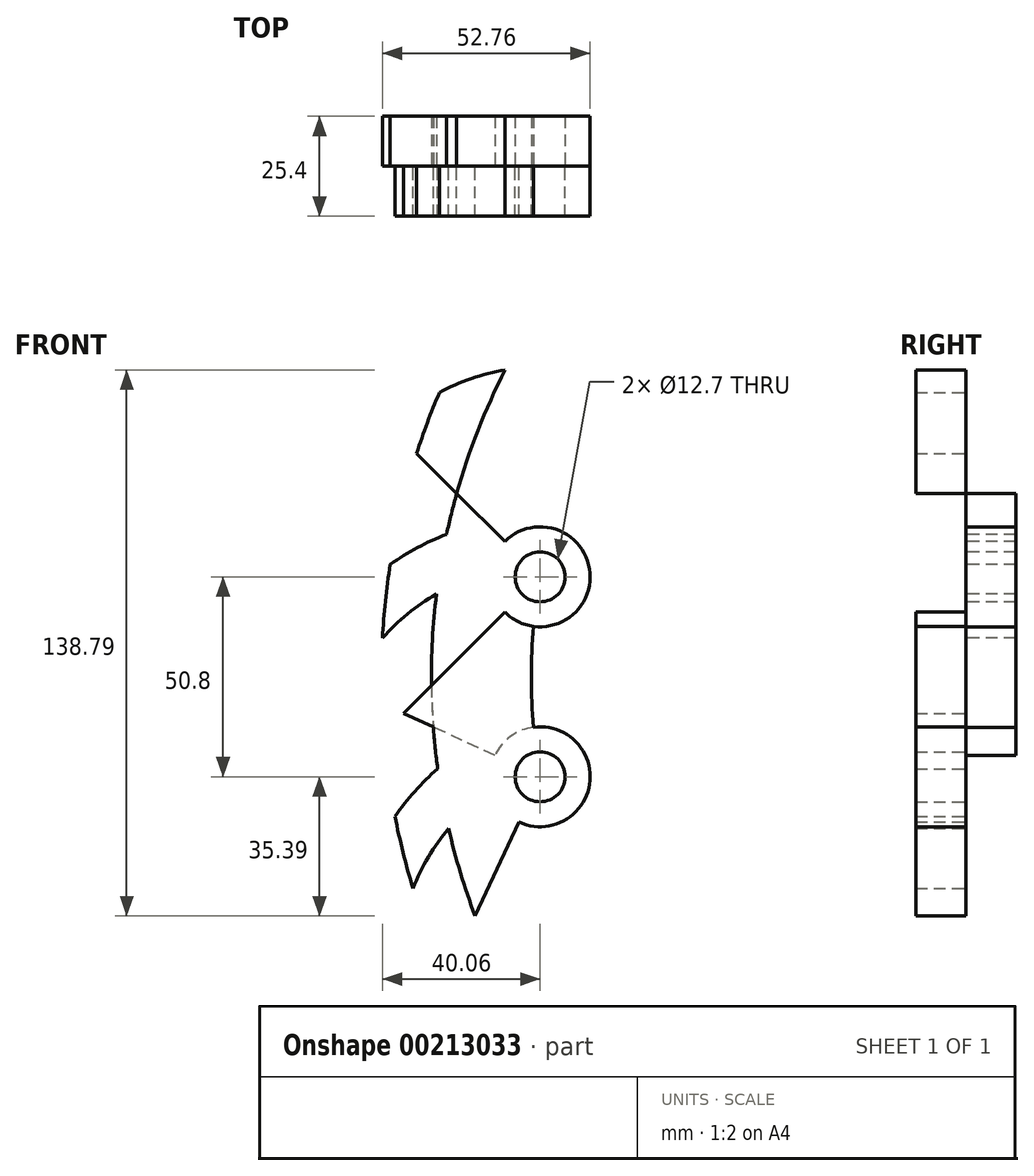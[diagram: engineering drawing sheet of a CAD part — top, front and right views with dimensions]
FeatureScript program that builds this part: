
annotation { "Feature Type Name" : "Feature", "Feature Type Description" : "" }
export const myFeature = defineFeature(function(context is Context, id is Id, definition is map)
    precondition{}
    {
        {
            var Q0;
            Q0=qCreatedBy(makeId("Front.planeOp"),FACE);
            var sketch = newSketch(context, id + "F0", { "sketchPlane" : qUnion([Q0])});
            skCircle(sketch, "E0", {"center": v(0, 0) * mm, "radius": 12.7 * mm});
            skCircle(sketch, "E1", {"center": v(0, 50.8) * mm, "radius": 12.7 * mm});
            skArc(sketch, "E2", {"start": v(0, 50.8) * mm, "mid": v(0, 0) * mm, "end": v(17.37, -47.74) * mm});
            skLineSegment(sketch, "E3", {"start": v(0, 50.8) * mm, "end": v(144.05, 25.4) * mm, "construction": true});
            skLineSegment(sketch, "E4", {"start": v(144.05, 25.4) * mm, "end": v(0, 0) * mm, "construction": true});
            skLineSegment(sketch, "E5", {"start": v(144.05, 25.4) * mm, "end": v(-15.62, -66.79) * mm, "construction": true});
            skArc(sketch, "E6", {"start": v(-4.62, -60.44) * mm, "mid": v(-11.07, -48.15) * mm, "end": v(-16.5, -35.39) * mm, "construction": true});
            skArc(sketch, "E7", {"start": v(-15.62, -66.79) * mm, "mid": v(-19.88, -58.97) * mm, "end": v(-23.76, -50.96) * mm, "construction": true});
            skLineSegment(sketch, "E8", {"start": v(0, 0) * mm, "end": v(0, 50.8) * mm, "construction": true});
            skLineSegment(sketch, "E9", {"start": v(0, 50.8) * mm, "end": v(-58.55, 109.35) * mm});
            skLineSegment(sketch, "E10", {"start": v(0, 50.8) * mm, "end": v(-62.14, -11.34) * mm});
            skLineSegment(sketch, "E11", {"start": v(0, 0) * mm, "end": v(-80.33, 37.46) * mm});
            skLineSegment(sketch, "E12", {"start": v(0, 0) * mm, "end": v(-37.7, -80.86) * mm});
            skArc(sketch, "E13", {"start": v(-21.18, 71.98) * mm, "mid": v(-15.8, 88) * mm, "end": v(-8.88, 103.4) * mm});
            skArc(sketch, "E14", {"start": v(-16.5, -35.39) * mm, "mid": v(-27.46, 17.92) * mm, "end": v(-21.18, 71.98) * mm});
            skArc(sketch, "E15", {"start": v(-31.37, 82.17) * mm, "mid": v(-25.13, 98.68) * mm, "end": v(-17.35, 114.52) * mm});
            skArc(sketch, "E16", {"start": v(-23.76, -50.96) * mm, "mid": v(-40.02, 14.89) * mm, "end": v(-31.37, 82.17) * mm});
            skArc(sketch, "E17", {"start": v(-32.32, -28.34) * mm, "mid": v(-28.41, -20.37) * mm, "end": v(-23.24, -13.16) * mm});
            skArc(sketch, "E18", {"start": v(-36.88, -10.08) * mm, "mid": v(-31.83, -3.68) * mm, "end": v(-26.03, 2.04) * mm});
            skArc(sketch, "E19.1.0", {"start": v(-40.06, 35.22) * mm, "mid": v(-33.66, 41.37) * mm, "end": v(-26.33, 46.39) * mm});
            skArc(sketch, "E19.1.1", {"start": v(-38.1, 53.94) * mm, "mid": v(-31.17, 58.22) * mm, "end": v(-23.76, 61.62) * mm});
            skArc(sketch, "E19.2.0", {"start": v(-25.6, 97.6) * mm, "mid": v(-17.48, 101.2) * mm, "end": v(-8.88, 103.4) * mm});
            skArc(sketch, "E19.2.1", {"start": v(-17.35, 114.52) * mm, "mid": v(-9.37, 116.17) * mm, "end": v(-1.25, 116.83) * mm});
            skLineSegment(sketch, "E19.anchor1", {"start": v(144.05, 25.4) * mm, "end": v(-32.32, -28.34) * mm, "construction": true});
            skLineSegment(sketch, "E19.anchor2", {"start": v(144.05, 25.4) * mm, "end": v(-25.6, 97.6) * mm, "construction": true});
            skArc(sketch, "E20", {"start": v(-8.88, 103.4) * mm, "mid": v(-5.22, 110.2) * mm, "end": v(-1.25, 116.83) * mm});
            skArc(sketch, "E21", {"start": v(-17.35, 114.52) * mm, "mid": v(-9.23, 127.87) * mm, "end": v(0, 140.48) * mm, "construction": true});
            skArc(sketch, "E22", {"start": v(-1.25, 116.83) * mm, "mid": v(8.95, 131.32) * mm, "end": v(20.6, 144.69) * mm, "construction": true});
            skCircle(sketch, "E23", {"center": v(0, 0) * mm, "radius": 6.35 * mm});
            skCircle(sketch, "E24", {"center": v(0, 50.8) * mm, "radius": 6.35 * mm});
            skSolve(sketch);
        }
        {
            var Q0;
            {var subQ2=sQuery(id+"F0.wireOp",EDGE,"E19.2.0");Q0=makeQuery(id+"F0.imprint","IMPRINT",FACE,{"disambiguationData":[TD([[makeQuery(id+"F0.imprint","IMPRINT",EDGE,{"derivedFrom":subQ2}),1.0]])]});}
            var Q1;
            {var subQ5=sQuery(id+"F0.wireOp",EDGE,"E17");Q1=makeQuery(id+"F0.imprint","IMPRINT",FACE,{"disambiguationData":[TD([[makeQuery(id+"F0.imprint","IMPRINT",EDGE,{"derivedFrom":subQ5}),-1.0]])]});}
            var Q2;
            {var subQ1=sQuery(id+"F0.wireOp",EDGE,"E12");var subQ3=sQuery(id+"F0.wireOp",EDGE,"E0");var subQ4=makeQuery(id+"F0.imprint","INTERSECT",VERTEX,{"derivedFrom":[subQ3,subQ1]});Q2=makeQuery(id+"F0.imprint","IMPRINT",FACE,{"disambiguationData":[TD([[makeQuery(id+"F0.imprint","IMPRINT",EDGE,{"disambiguationData":[TD([[subQ4,1.0]])],"derivedFrom":subQ3}),-1.0]])]});}
            var Q3;
            {var subQ0=sQuery(id+"F0.wireOp",EDGE,"E18");Q3=makeQuery(id+"F0.imprint","IMPRINT",FACE,{"disambiguationData":[TD([[makeQuery(id+"F0.imprint","IMPRINT",EDGE,{"derivedFrom":subQ0}),1.0]])]});}
            var Q4;
            {var subQ0=sQuery(id+"F0.wireOp",EDGE,"E2");var subQ1=sQuery(id+"F0.wireOp",EDGE,"E0");var subQ2=makeQuery(id+"F0.imprint","INTERSECT",VERTEX,{"disambiguationData":[OD(1.0)],"derivedFrom":[subQ1,subQ0]});Q4=makeQuery(id+"F0.imprint","IMPRINT",FACE,{"disambiguationData":[TD([[makeQuery(id+"F0.imprint","IMPRINT",EDGE,{"disambiguationData":[TD([[subQ2,-1.0]])],"derivedFrom":subQ1}),-1.0]])]});}
            var Q5;
            {var subQ0=sQuery(id+"F0.wireOp",EDGE,"E14");var subQ1=sQuery(id+"F0.wireOp",EDGE,"E10");var subQ2=makeQuery(id+"F0.imprint","INTERSECT",VERTEX,{"derivedFrom":[subQ1,subQ0]});Q5=makeQuery(id+"F0.imprint","IMPRINT",FACE,{"disambiguationData":[TD([[makeQuery(id+"F0.imprint","IMPRINT",EDGE,{"disambiguationData":[TD([[subQ2,-1.0]])],"derivedFrom":subQ1}),1.0]])]});}
            var Q6;
            {var subQ2=sQuery(id+"F0.wireOp",EDGE,"E19.2.0");Q6=makeQuery(id+"F0.imprint","IMPRINT",FACE,{"disambiguationData":[TD([[makeQuery(id+"F0.imprint","IMPRINT",EDGE,{"derivedFrom":subQ2}),1.0]])]});}
            var Q7;
            {var subQ0=sQuery(id+"F0.wireOp",EDGE,"E12");var subQ1=sQuery(id+"F0.wireOp",EDGE,"E0");var subQ2=makeQuery(id+"F0.imprint","INTERSECT",VERTEX,{"derivedFrom":[subQ1,subQ0]});Q7=makeQuery(id+"F0.imprint","IMPRINT",FACE,{"disambiguationData":[TD([[makeQuery(id+"F0.imprint","IMPRINT",EDGE,{"disambiguationData":[TD([[subQ2,1.0]])],"derivedFrom":subQ1}),1.0]])]});}
            var Q8;
            {var subQ0=sQuery(id+"F0.wireOp",EDGE,"E2");var subQ1=sQuery(id+"F0.wireOp",EDGE,"E0");var subQ2=makeQuery(id+"F0.imprint","INTERSECT",VERTEX,{"disambiguationData":[OD(1.0)],"derivedFrom":[subQ1,subQ0]});Q8=makeQuery(id+"F0.imprint","IMPRINT",FACE,{"disambiguationData":[TD([[makeQuery(id+"F0.imprint","IMPRINT",EDGE,{"disambiguationData":[TD([[subQ2,-1.0]])],"derivedFrom":subQ1}),1.0]])]});}
            var Q9;
            {var subQ0=sQuery(id+"F0.wireOp",EDGE,"E2");var subQ1=sQuery(id+"F0.wireOp",EDGE,"E0");var subQ2=makeQuery(id+"F0.imprint","INTERSECT",VERTEX,{"disambiguationData":[OD(0.0)],"derivedFrom":[subQ1,subQ0]});Q9=makeQuery(id+"F0.imprint","IMPRINT",FACE,{"disambiguationData":[TD([[makeQuery(id+"F0.imprint","IMPRINT",EDGE,{"disambiguationData":[TD([[subQ2,-1.0]])],"derivedFrom":subQ1}),1.0]])]});}
            var Q10;
            {var subQ0=sQuery(id+"F0.wireOp",EDGE,"E2");var subQ1=sQuery(id+"F0.wireOp",EDGE,"E0");var subQ2=makeQuery(id+"F0.imprint","INTERSECT",VERTEX,{"disambiguationData":[OD(0.0)],"derivedFrom":[subQ1,subQ0]});Q10=makeQuery(id+"F0.imprint","IMPRINT",FACE,{"disambiguationData":[TD([[makeQuery(id+"F0.imprint","IMPRINT",EDGE,{"disambiguationData":[TD([[subQ2,1.0]])],"derivedFrom":subQ1}),1.0]])]});}
            extrude(context, id + "F1", {"entities" : qUnion([Q0, Q1, Q2, Q3, Q4, Q5, Q6, Q7, Q8, Q9, Q10]), "depth" : 12.7 * mm});
        }
        {
            var Q0;
            {var subQ4=sQuery(id+"F0.wireOp",EDGE,"E1");var subQ6=sQuery(id+"F0.wireOp",EDGE,"E9");var subQ8=makeQuery(id+"F0.imprint","INTERSECT",VERTEX,{"derivedFrom":[subQ4,subQ6]});Q0=makeQuery(id+"F0.imprint","IMPRINT",FACE,{"disambiguationData":[TD([[makeQuery(id+"F0.imprint","IMPRINT",EDGE,{"disambiguationData":[TD([[subQ8,-1.0]])],"derivedFrom":subQ4}),-1.0]])]});}
            var Q1;
            {var subQ0=sQuery(id+"F0.wireOp",EDGE,"E2");var subQ1=sQuery(id+"F0.wireOp",EDGE,"E0");var subQ2=makeQuery(id+"F0.imprint","INTERSECT",VERTEX,{"disambiguationData":[OD(1.0)],"derivedFrom":[subQ1,subQ0]});Q1=makeQuery(id+"F0.imprint","IMPRINT",FACE,{"disambiguationData":[TD([[makeQuery(id+"F0.imprint","IMPRINT",EDGE,{"disambiguationData":[TD([[subQ2,-1.0]])],"derivedFrom":subQ1}),-1.0]])]});}
            var Q2;
            {var subQ0=sQuery(id+"F0.wireOp",EDGE,"E19.1.1");Q2=makeQuery(id+"F0.imprint","IMPRINT",FACE,{"disambiguationData":[TD([[makeQuery(id+"F0.imprint","IMPRINT",EDGE,{"derivedFrom":subQ0}),1.0]])]});}
            var Q3;
            {var subQ0=sQuery(id+"F0.wireOp",EDGE,"E13");Q3=makeQuery(id+"F0.imprint","IMPRINT",FACE,{"disambiguationData":[TD([[makeQuery(id+"F0.imprint","IMPRINT",EDGE,{"derivedFrom":subQ0}),1.0]])]});}
            var Q4;
            {var subQ4=sQuery(id+"F0.wireOp",EDGE,"E15");Q4=makeQuery(id+"F0.imprint","IMPRINT",FACE,{"disambiguationData":[TD([[makeQuery(id+"F0.imprint","IMPRINT",EDGE,{"derivedFrom":subQ4}),-1.0]])]});}
            var Q5;
            {var subQ0=sQuery(id+"F0.wireOp",EDGE,"E2");var subQ1=sQuery(id+"F0.wireOp",EDGE,"E1");var subQ2=makeQuery(id+"F0.imprint","INTERSECT",VERTEX,{"derivedFrom":[subQ1,subQ0]});Q5=makeQuery(id+"F0.imprint","IMPRINT",FACE,{"disambiguationData":[TD([[makeQuery(id+"F0.imprint","IMPRINT",EDGE,{"disambiguationData":[TD([[subQ2,1.0]])],"derivedFrom":subQ1}),1.0]])]});}
            var Q6;
            {var subQ0=sQuery(id+"F0.wireOp",EDGE,"E9");var subQ1=sQuery(id+"F0.wireOp",EDGE,"E1");var subQ2=makeQuery(id+"F0.imprint","INTERSECT",VERTEX,{"derivedFrom":[subQ1,subQ0]});Q6=makeQuery(id+"F0.imprint","IMPRINT",FACE,{"disambiguationData":[TD([[makeQuery(id+"F0.imprint","IMPRINT",EDGE,{"disambiguationData":[TD([[subQ2,-1.0]])],"derivedFrom":subQ1}),1.0]])]});}
            var Q7;
            {var subQ0=sQuery(id+"F0.wireOp",EDGE,"E9");var subQ1=sQuery(id+"F0.wireOp",EDGE,"E1");var subQ2=makeQuery(id+"F0.imprint","INTERSECT",VERTEX,{"derivedFrom":[subQ1,subQ0]});Q7=makeQuery(id+"F0.imprint","IMPRINT",FACE,{"disambiguationData":[TD([[makeQuery(id+"F0.imprint","IMPRINT",EDGE,{"disambiguationData":[TD([[subQ2,1.0]])],"derivedFrom":subQ1}),1.0]])]});}
            extrude(context, id + "F2", {"entities" : qUnion([Q0, Q1, Q2, Q3, Q4, Q5, Q6, Q7]), "oppositeDirection" : true, "depth" : 12.7 * mm});
        }
    });
